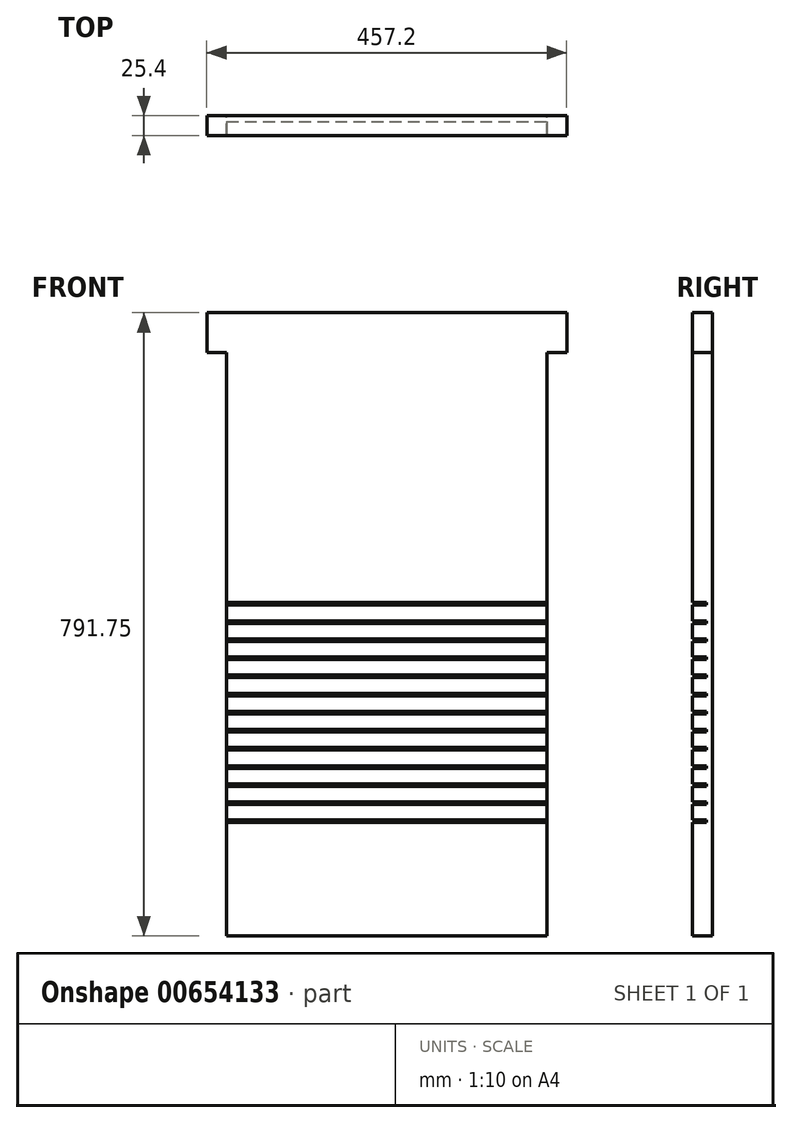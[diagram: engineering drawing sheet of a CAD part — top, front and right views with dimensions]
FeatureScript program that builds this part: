
annotation { "Feature Type Name" : "Feature", "Feature Type Description" : "" }
export const myFeature = defineFeature(function(context is Context, id is Id, definition is map)
    precondition{}
    {
        {
            var Q0;
            Q0=qCreatedBy(makeId("Front.planeOp"),FACE);
            var sketch = newSketch(context, id + "F0", { "sketchPlane" : qUnion([Q0])});
            skLineSegment(sketch, "E0", {"start": v(218.02, 487.6) * mm, "end": v(218.02, -253.35) * mm});
            skLineSegment(sketch, "E1", {"start": v(218.02, -253.35) * mm, "end": v(-188.38, -253.35) * mm});
            skLineSegment(sketch, "E2", {"start": v(-188.38, -253.35) * mm, "end": v(-188.38, 487.6) * mm});
            skLineSegment(sketch, "E3", {"start": v(-188.38, 487.6) * mm, "end": v(-213.78, 487.6) * mm});
            skLineSegment(sketch, "E4", {"start": v(-213.78, 487.6) * mm, "end": v(-213.78, 538.4) * mm});
            skLineSegment(sketch, "E5", {"start": v(-213.78, 538.4) * mm, "end": v(243.42, 538.4) * mm});
            skLineSegment(sketch, "E6", {"start": v(243.42, 538.4) * mm, "end": v(243.42, 487.6) * mm});
            skLineSegment(sketch, "E7", {"start": v(243.42, 487.6) * mm, "end": v(218.02, 487.6) * mm});
            skSolve(sketch);
        }
        {
            var Q0;
            Q0=qSketchRegion(id+"F0",true);
            extrude(context, id + "F1", {"entities" : qUnion([Q0]), "depth" : 25.4 * mm, "offsetDistance" : 25.4 * mm});
        }
        {
            var Q0;
            Q0=makeQuery(id+"F1.opExtrude","CAP_FACE",FACE,{"disambiguationData":[OSD([sQuery(id+"F0.wireOp",EDGE,"nucxnGlp-mwWK-UEnA-M79N-NN6MjnWQ4m8z"),sQuery(id+"F0.wireOp",EDGE,"E0"),sQuery(id+"F0.wireOp",EDGE,"E1"),sQuery(id+"F0.wireOp",EDGE,"E2")])],"isStart":false});
            var sketch = newSketch(context, id + "F2", { "sketchPlane" : qUnion([Q0])});
            skLineSegment(sketch, "E8", {"start": v(-188.38, -109.3) * mm, "end": v(218.02, -109.3) * mm});
            skLineSegment(sketch, "E9", {"start": v(-188.38, 170.1) * mm, "end": v(218.02, 170.1) * mm});
            skLineSegment(sketch, "E10", {"start": v(-188.38, -106.12) * mm, "end": v(218.02, -106.12) * mm});
            skLineSegment(sketch, "E11", {"start": v(218.02, 166.93) * mm, "end": v(-188.38, 166.93) * mm});
            skLineSegment(sketch, "E12", {"start": v(218.02, -86.28) * mm, "end": v(-188.38, -86.28) * mm});
            skLineSegment(sketch, "E13", {"start": v(-188.38, -83.1) * mm, "end": v(218.02, -83.1) * mm});
            skLineSegment(sketch, "E14", {"start": v(218.02, -40.24) * mm, "end": v(-188.38, -40.24) * mm});
            skLineSegment(sketch, "E15", {"start": v(-188.38, -37.07) * mm, "end": v(218.02, -37.07) * mm});
            skLineSegment(sketch, "E16", {"start": v(218.02, -17.22) * mm, "end": v(-188.38, -17.22) * mm});
            skLineSegment(sketch, "E17", {"start": v(-188.38, -14.05) * mm, "end": v(218.02, -14.05) * mm});
            skLineSegment(sketch, "E18", {"start": v(218.02, 5.8) * mm, "end": v(-188.38, 5.8) * mm});
            skLineSegment(sketch, "E19", {"start": v(-188.38, 8.97) * mm, "end": v(218.02, 8.97) * mm});
            skLineSegment(sketch, "E20", {"start": v(218.02, 28.81) * mm, "end": v(-188.38, 28.81) * mm});
            skLineSegment(sketch, "E21", {"start": v(-188.38, 31.99) * mm, "end": v(218.02, 31.99) * mm});
            skLineSegment(sketch, "E22", {"start": v(218.02, 51.83) * mm, "end": v(-188.38, 51.83) * mm});
            skLineSegment(sketch, "E23", {"start": v(-188.38, 55) * mm, "end": v(218.02, 55) * mm});
            skLineSegment(sketch, "E24", {"start": v(218.02, 74.85) * mm, "end": v(-188.38, 74.85) * mm});
            skLineSegment(sketch, "E25", {"start": v(-188.38, 78.03) * mm, "end": v(218.02, 78.03) * mm});
            skLineSegment(sketch, "E26", {"start": v(218.02, 97.87) * mm, "end": v(-188.38, 97.87) * mm});
            skLineSegment(sketch, "E27", {"start": v(-188.38, 101.04) * mm, "end": v(218.02, 101.04) * mm});
            skLineSegment(sketch, "E28", {"start": v(218.02, 120.89) * mm, "end": v(-188.38, 120.89) * mm});
            skLineSegment(sketch, "E29", {"start": v(-188.38, 124.06) * mm, "end": v(218.02, 124.06) * mm});
            skLineSegment(sketch, "E30", {"start": v(218.02, 143.9) * mm, "end": v(-188.38, 143.9) * mm});
            skLineSegment(sketch, "E31", {"start": v(-188.38, 147.08) * mm, "end": v(218.02, 147.08) * mm});
            skLineSegment(sketch, "E32", {"start": v(-188.38, 166.93) * mm, "end": v(-188.38, 147.08) * mm});
            skLineSegment(sketch, "E33", {"start": v(-188.38, 143.9) * mm, "end": v(-188.38, 124.06) * mm});
            skLineSegment(sketch, "E34", {"start": v(-188.38, 120.89) * mm, "end": v(-188.38, 101.04) * mm});
            skLineSegment(sketch, "E35", {"start": v(-188.38, 97.87) * mm, "end": v(-188.38, 78.03) * mm});
            skLineSegment(sketch, "E36", {"start": v(-188.38, 74.85) * mm, "end": v(-188.38, 55) * mm});
            skLineSegment(sketch, "E37", {"start": v(-188.38, 51.83) * mm, "end": v(-188.38, 31.99) * mm});
            skLineSegment(sketch, "E38", {"start": v(-188.38, 28.81) * mm, "end": v(-188.38, 8.97) * mm});
            skLineSegment(sketch, "E39", {"start": v(-188.38, 5.8) * mm, "end": v(-188.38, -14.05) * mm});
            skLineSegment(sketch, "E40", {"start": v(-188.38, -17.22) * mm, "end": v(-188.38, -37.07) * mm});
            skLineSegment(sketch, "E41", {"start": v(-188.38, -60.09) * mm, "end": v(218.02, -60.09) * mm});
            skLineSegment(sketch, "E42", {"start": v(218.02, -63.26) * mm, "end": v(-188.38, -63.26) * mm});
            skLineSegment(sketch, "E43", {"start": v(-188.38, -83.1) * mm, "end": v(-188.38, -63.26) * mm});
            skLineSegment(sketch, "E44", {"start": v(-188.38, -60.09) * mm, "end": v(-188.38, -40.24) * mm});
            skLineSegment(sketch, "E45", {"start": v(-188.38, -86.28) * mm, "end": v(-188.38, -106.12) * mm});
            skSolve(sketch);
        }
        {
            var Q0;
            {var subQ0=sQuery(id+"F2.wireOp",EDGE,"E9");Q0=makeQuery(id+"F2.imprint","IMPRINT",FACE,{"disambiguationData":[TD([[makeQuery(id+"F2.imprint","IMPRINT",EDGE,{"derivedFrom":subQ0}),-1.0]])]});}
            var Q1;
            {var subQ0=sQuery(id+"F2.wireOp",EDGE,"E30");Q1=makeQuery(id+"F2.imprint","IMPRINT",FACE,{"disambiguationData":[TD([[makeQuery(id+"F2.imprint","IMPRINT",EDGE,{"derivedFrom":subQ0}),-1.0]])]});}
            var Q2;
            {var subQ0=sQuery(id+"F2.wireOp",EDGE,"E28");Q2=makeQuery(id+"F2.imprint","IMPRINT",FACE,{"disambiguationData":[TD([[makeQuery(id+"F2.imprint","IMPRINT",EDGE,{"derivedFrom":subQ0}),-1.0]])]});}
            var Q3;
            {var subQ0=sQuery(id+"F2.wireOp",EDGE,"E18");Q3=makeQuery(id+"F2.imprint","IMPRINT",FACE,{"disambiguationData":[TD([[makeQuery(id+"F2.imprint","IMPRINT",EDGE,{"derivedFrom":subQ0}),-1.0]])]});}
            var Q4;
            {var subQ0=sQuery(id+"F2.wireOp",EDGE,"E24");Q4=makeQuery(id+"F2.imprint","IMPRINT",FACE,{"disambiguationData":[TD([[makeQuery(id+"F2.imprint","IMPRINT",EDGE,{"derivedFrom":subQ0}),-1.0]])]});}
            var Q5;
            {var subQ0=sQuery(id+"F2.wireOp",EDGE,"E22");Q5=makeQuery(id+"F2.imprint","IMPRINT",FACE,{"disambiguationData":[TD([[makeQuery(id+"F2.imprint","IMPRINT",EDGE,{"derivedFrom":subQ0}),-1.0]])]});}
            var Q6;
            {var subQ0=sQuery(id+"F2.wireOp",EDGE,"E26");Q6=makeQuery(id+"F2.imprint","IMPRINT",FACE,{"disambiguationData":[TD([[makeQuery(id+"F2.imprint","IMPRINT",EDGE,{"derivedFrom":subQ0}),-1.0]])]});}
            var Q7;
            {var subQ0=sQuery(id+"F2.wireOp",EDGE,"E20");Q7=makeQuery(id+"F2.imprint","IMPRINT",FACE,{"disambiguationData":[TD([[makeQuery(id+"F2.imprint","IMPRINT",EDGE,{"derivedFrom":subQ0}),-1.0]])]});}
            var Q8;
            {var subQ0=sQuery(id+"F2.wireOp",EDGE,"E16");Q8=makeQuery(id+"F2.imprint","IMPRINT",FACE,{"disambiguationData":[TD([[makeQuery(id+"F2.imprint","IMPRINT",EDGE,{"derivedFrom":subQ0}),-1.0]])]});}
            var Q9;
            {var subQ0=sQuery(id+"F2.wireOp",EDGE,"E14");Q9=makeQuery(id+"F2.imprint","IMPRINT",FACE,{"disambiguationData":[TD([[makeQuery(id+"F2.imprint","IMPRINT",EDGE,{"derivedFrom":subQ0}),-1.0]])]});}
            var Q10;
            {var subQ0=sQuery(id+"F2.wireOp",EDGE,"E41");Q10=makeQuery(id+"F2.imprint","IMPRINT",FACE,{"disambiguationData":[TD([[makeQuery(id+"F2.imprint","IMPRINT",EDGE,{"derivedFrom":subQ0}),-1.0]])]});}
            var Q11;
            {var subQ0=sQuery(id+"F2.wireOp",EDGE,"E12");Q11=makeQuery(id+"F2.imprint","IMPRINT",FACE,{"disambiguationData":[TD([[makeQuery(id+"F2.imprint","IMPRINT",EDGE,{"derivedFrom":subQ0}),-1.0]])]});}
            var Q12;
            {var subQ0=sQuery(id+"F2.wireOp",EDGE,"oKOZSNRP-SMp8-eb1Z-5gQ2-SgGibsilJWI4");Q12=makeQuery(id+"F2.imprint","IMPRINT",FACE,{"disambiguationData":[TD([[makeQuery(id+"F2.imprint","IMPRINT",EDGE,{"derivedFrom":subQ0}),1.0]])]});}
            var Q13;
            {var subQ0=sQuery(id+"F2.wireOp",EDGE,"E8");Q13=makeQuery(id+"F2.imprint","IMPRINT",FACE,{"disambiguationData":[TD([[makeQuery(id+"F2.imprint","IMPRINT",EDGE,{"derivedFrom":subQ0}),1.0]])]});}
            extrude(context, id + "F3", {"entities" : qUnion([Q0, Q1, Q2, Q3, Q4, Q5, Q6, Q7, Q8, Q9, Q10, Q11, Q12, Q13]), "operationType" : NewBodyOperationType.REMOVE, "oppositeDirection" : true, "depth" : 17.46 * mm, "offsetDistance" : 25.4 * mm});
        }
    });
